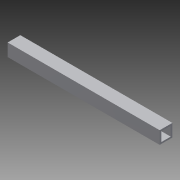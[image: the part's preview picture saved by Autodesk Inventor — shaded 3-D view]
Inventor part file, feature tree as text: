
AUTODESK INVENTOR PART (.ipt)
format: ipt  version: 2014 (Build 180170000, 170)  size: 91,648 bytes
history: native  units: in
note: dims shown in document units (in); Inventor stores cm internally (conversion verified against a paired STEP export)
features: extrude x1, sketch x1
ambient origin geometry x8: Origin, YZ Plane, XZ Plane, XY Plane, X Axis, Y Axis, Z Axis, Center Point
bodies: Solid1 (feature_tree)
feature tree (2):
  extrude  "Extrusion1"  Depth=1.0in
  sketch  "Sketch1"  dims[d0=1.0in d1=1.0in d2=0.125in d3=12.0in d4=0.0in]
